FCSTD DOCUMENT  (FreeCAD 2023.131R26244 +5365 (Git))
Label: Workstation
License: All rights reserved
LicenseURL: http://en.wikipedia.org/wiki/All_rights_reserved
objects: Sketcher::SketchObject×1, PartDesign::Body×1, App::Part×1
note: 3 computed .brp shape members not serialized (recipe doc carries the construction recipe); baked Part::Feature solids carry a one-line shape summary decoded from their .brp

FEATURE [Sketcher::SketchObject] Sketch
  ArcFitTolerance = 1e-06
  AttachmentSupport = -> [XY_Plane]
  ExternalBSplineMaxDegree = 5
  ExternalBSplineTolerance = 0.0001
  FixShape = 1
  FullyConstrained = true
  InternalTolerance = 1e-06
  InvalidShape = false
  MakeInternals = false
  MapMode = 5
  Support = -> [XY_Plane]
  TreeRank = 14
  ValidateShape = false
  sketch-geometry (6):
    g0: LineSegment StartX=0 StartY=0 StartZ=0 EndX=0 EndY=-1981.2 EndZ=0
    g1: LineSegment StartX=0 StartY=-1981.2 StartZ=0 EndX=698.5 EndY=-1981.2 EndZ=0
    g2: LineSegment StartX=698.5 StartY=-1981.2 StartZ=0 EndX=698.5 EndY=-762 EndZ=0
    g3: LineSegment StartX=698.5 StartY=-762 StartZ=0 EndX=2032 EndY=-762 EndZ=0
    g4: LineSegment StartX=2032 StartY=-762 StartZ=0 EndX=2032 EndY=0 EndZ=0
    g5: LineSegment StartX=2032 StartY=0 StartZ=0 EndX=0 EndY=0 EndZ=0
  constraints (17):
    c: Coincident(g0,g-1)
    c: PointOnObject(g0,g-2)
    c: Coincident(g1,g0)
    c: Horizontal(g1)
    c: Coincident(g2,g1)
    c: Vertical(g2)
    c: Coincident(g3,g2)
    c: Horizontal(g3)
    c: Coincident(g4,g3)
    c: PointOnObject(g4,g-1)
    c: Vertical(g4)
    c: Coincident(g5,g4)
    c: Coincident(g5,g0)
    c: DistanceX(g5,g5) = 2032
    c: DistanceY(g0,g0) = 1981.2
    c: DistanceY(g4,g4) = 762
    c: DistanceX(g1,g1) = 698.5
FEATURE [PartDesign::Body] Body
  AutoGroupSolids = false
  ClaimAllChildren = false
  ExportMode = 0
  FixShape = 1
  Group = -> [Sketch]
  InvalidShape = false
  Origin = -> Origin001
  TreeRank = 13
  ValidateShape = false
  _ExportChildren = -> [Sketch]
  _GroupVersion = 1
FEATURE [App::Part] Part  label="Workstation-Part"
  ClaimAllChildren = false
  ExportMode = 1
  Group = -> [Body]
  Origin = -> Origin
  TreeRank = 3
  _ExportChildren = -> [Body]
  _GroupVersion = 1
